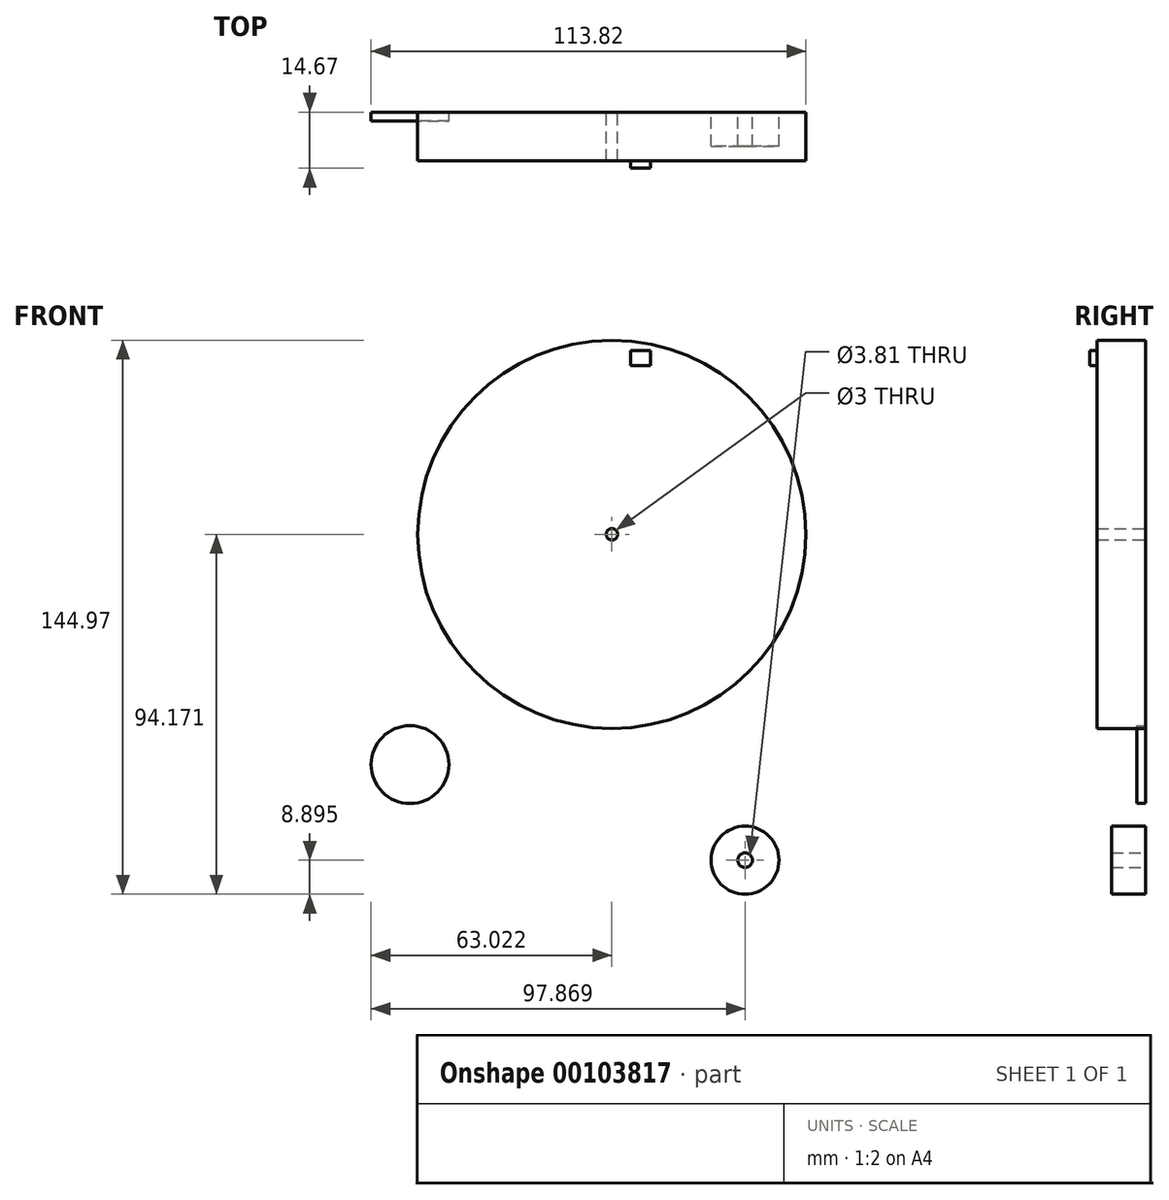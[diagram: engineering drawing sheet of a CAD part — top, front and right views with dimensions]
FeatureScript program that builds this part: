
annotation { "Feature Type Name" : "Feature", "Feature Type Description" : "" }
export const myFeature = defineFeature(function(context is Context, id is Id, definition is map)
    precondition{}
    {
        {
            var Q0;
            Q0=qCreatedBy(makeId("Front.planeOp"),FACE);
            var sketch = newSketch(context, id + "F0", { "sketchPlane" : qUnion([Q0])});
            skCircle(sketch, "E0", {"center": v(5.1, 35.22) * mm, "radius": 50.8 * mm});
            skCircle(sketch, "E1", {"center": v(5.1, 35.22) * mm, "radius": 1.5 * mm});
            skLineSegment(sketch, "E2.bottom", {"start": v(15.24, 83.37) * mm, "end": v(10.03, 83.37) * mm});
            skLineSegment(sketch, "E2.top", {"start": v(15.24, 79.4) * mm, "end": v(10.03, 79.4) * mm});
            skLineSegment(sketch, "E2.left", {"start": v(15.24, 83.37) * mm, "end": v(15.24, 79.4) * mm});
            skLineSegment(sketch, "E2.right", {"start": v(10.03, 83.37) * mm, "end": v(10.03, 79.4) * mm});
            skCircle(sketch, "E3", {"center": v(-47.75, -25.05) * mm, "radius": 10.18 * mm});
            skCircle(sketch, "E4", {"center": v(39.94, -50.06) * mm, "radius": 8.9 * mm});
            skCircle(sketch, "E5", {"center": v(39.94, -50.06) * mm, "radius": 1.9 * mm});
            skSolve(sketch);
        }
        {
            var Q0;
            Q0=makeQuery(id+"F0.imprint","IMPRINT",FACE,{"disambiguationData":[TD([[makeQuery(id+"F0.imprint","IMPRINT",EDGE,{"derivedFrom":sQuery(id+"F0.wireOp",EDGE,"E0")}),1.0]])]});
            var Q1;
            Q1=makeQuery(id+"F0.imprint","IMPRINT",FACE,{"disambiguationData":[TD([[makeQuery(id+"F0.imprint","IMPRINT",EDGE,{"derivedFrom":sQuery(id+"F0.wireOp",EDGE,"E2.bottom")}),1.0]])]});
            extrude(context, id + "F1", {"entities" : qUnion([Q0, Q1]), "depth" : 12.7 * mm});
        }
        {
            var Q0;
            Q0=makeQuery(id+"F0.imprint","IMPRINT",FACE,{"disambiguationData":[TD([[makeQuery(id+"F0.imprint","IMPRINT",EDGE,{"derivedFrom":sQuery(id+"F0.wireOp",EDGE,"E2.bottom")}),1.0]])]});
            extrude(context, id + "F2", {"entities" : qUnion([Q0]), "operationType" : NewBodyOperationType.ADD, "depth" : 14.67 * mm});
        }
        {
            var Q0;
            Q0=makeQuery(id+"F0.imprint","IMPRINT",FACE,{"disambiguationData":[TD([[makeQuery(id+"F0.imprint","IMPRINT",EDGE,{"derivedFrom":sQuery(id+"F0.wireOp",EDGE,"E3")}),1.0]])]});
            extrude(context, id + "F3", {"entities" : qUnion([Q0]), "depth" : 2.3 * mm});
        }
        {
            var Q0;
            Q0=makeQuery(id+"F0.imprint","IMPRINT",FACE,{"disambiguationData":[TD([[makeQuery(id+"F0.imprint","IMPRINT",EDGE,{"derivedFrom":sQuery(id+"F0.wireOp",EDGE,"E4")}),1.0]])]});
            extrude(context, id + "F4", {"entities" : qUnion([Q0]), "depth" : 8.9 * mm});
        }
    });
